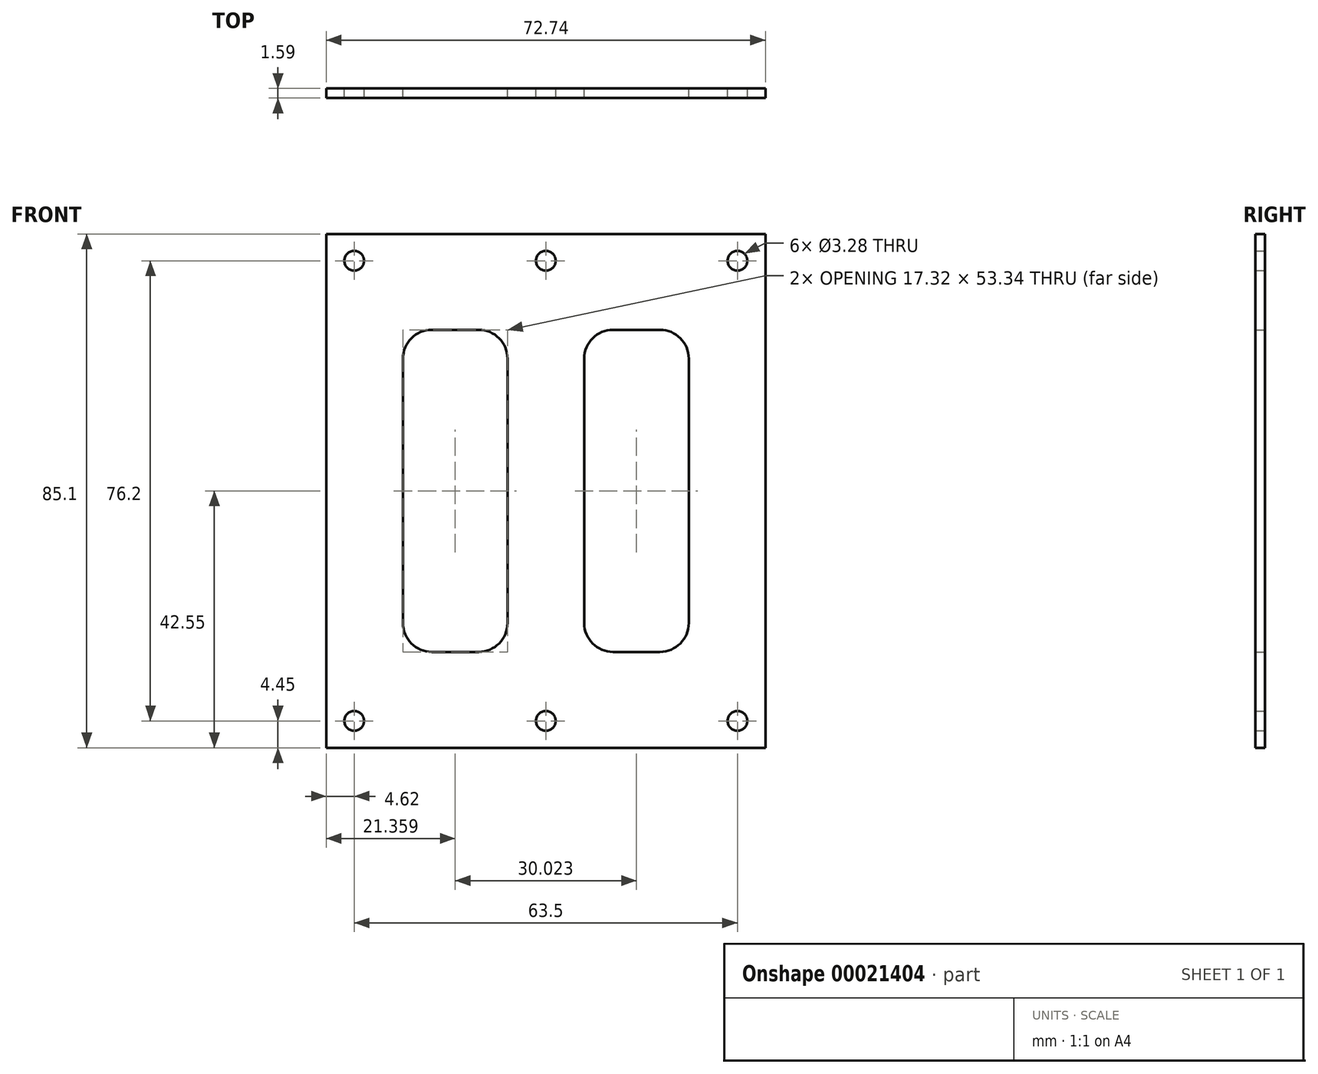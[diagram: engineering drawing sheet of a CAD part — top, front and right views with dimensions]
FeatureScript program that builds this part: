
annotation { "Feature Type Name" : "Feature", "Feature Type Description" : "" }
export const myFeature = defineFeature(function(context is Context, id is Id, definition is map)
    precondition{}
    {
        {
            var Q0;
            Q0=qCreatedBy(makeId("Front.planeOp"),FACE);
            var sketch = newSketch(context, id + "F0", { "sketchPlane" : qUnion([Q0])});
            skLineSegment(sketch, "E0.rect.bottom", {"start": v(36.37, 42.55) * mm, "end": v(-36.37, 42.55) * mm});
            skLineSegment(sketch, "E0.rect.top", {"start": v(36.37, -42.55) * mm, "end": v(-36.37, -42.55) * mm});
            skLineSegment(sketch, "E0.rect.left", {"start": v(36.37, 42.55) * mm, "end": v(36.37, -42.55) * mm});
            skLineSegment(sketch, "E0.rect.right", {"start": v(-36.37, 42.55) * mm, "end": v(-36.37, -42.55) * mm});
            skPoint(sketch, "E0.rect.middle", {"position": v(0, 0) * mm});
            skLineSegment(sketch, "E1.bottom", {"start": v(-23.67, 26.67) * mm, "end": v(-6.35, 26.67) * mm});
            skLineSegment(sketch, "E1.top", {"start": v(-23.67, -26.67) * mm, "end": v(-6.35, -26.67) * mm});
            skLineSegment(sketch, "E1.left", {"start": v(-23.67, 26.67) * mm, "end": v(-23.67, -26.67) * mm});
            skLineSegment(sketch, "E1.right", {"start": v(-6.35, 26.67) * mm, "end": v(-6.35, -26.67) * mm});
            skLineSegment(sketch, "E2.bottom", {"start": v(6.35, 26.67) * mm, "end": v(23.67, 26.67) * mm});
            skLineSegment(sketch, "E2.top", {"start": v(6.35, -26.67) * mm, "end": v(23.67, -26.67) * mm});
            skLineSegment(sketch, "E2.left", {"start": v(6.35, 26.67) * mm, "end": v(6.35, -26.67) * mm});
            skLineSegment(sketch, "E2.right", {"start": v(23.67, 26.67) * mm, "end": v(23.67, -26.67) * mm});
            skLineSegment(sketch, "E3", {"start": v(0, 0) * mm, "end": v(0, 48.78) * mm});
            skLineSegment(sketch, "E4", {"start": v(0, 0) * mm, "end": v(59.25, 0) * mm});
            skSolve(sketch);
        }
        {
            var Q0;
            {var subQ13=sQuery(id+"F0.wireOp",EDGE,"E0.rect.top");Q0=makeQuery(id+"F0.imprint","IMPRINT",FACE,{"disambiguationData":[TD([[makeQuery(id+"F0.imprint","IMPRINT",EDGE,{"derivedFrom":subQ13}),-1.0]])]});}
            var Q1;
            {var subQ7=sQuery(id+"F0.wireOp",EDGE,"E2.bottom");Q1=makeQuery(id+"F0.imprint","IMPRINT",FACE,{"disambiguationData":[TD([[makeQuery(id+"F0.imprint","IMPRINT",EDGE,{"derivedFrom":subQ7}),1.0]])]});}
            extrude(context, id + "F1", {"entities" : qUnion([Q0, Q1]), "depth" : 1.59 * mm});
        }
        {
            var Q0;
            Q0=makeQuery(id+"F1.opExtrude","SWEPT_EDGE",EDGE,{"disambiguationData":[OSD([sQuery(id+"F0.wireOp",EDGE,"E2.bottom"),sQuery(id+"F0.wireOp",EDGE,"E2.right")])]});
            var Q1;
            Q1=makeQuery(id+"F1.opExtrude","SWEPT_EDGE",EDGE,{"disambiguationData":[OSD([sQuery(id+"F0.wireOp",EDGE,"E2.top"),sQuery(id+"F0.wireOp",EDGE,"E2.right")])]});
            var Q2;
            Q2=makeQuery(id+"F1.opExtrude","SWEPT_EDGE",EDGE,{"disambiguationData":[OSD([sQuery(id+"F0.wireOp",EDGE,"E2.bottom"),sQuery(id+"F0.wireOp",EDGE,"E2.left")])]});
            var Q3;
            Q3=makeQuery(id+"F1.opExtrude","SWEPT_EDGE",EDGE,{"disambiguationData":[OSD([sQuery(id+"F0.wireOp",EDGE,"E2.top"),sQuery(id+"F0.wireOp",EDGE,"E2.left")])]});
            var Q4;
            Q4=makeQuery(id+"F1.opExtrude","SWEPT_EDGE",EDGE,{"disambiguationData":[OSD([sQuery(id+"F0.wireOp",EDGE,"E1.top"),sQuery(id+"F0.wireOp",EDGE,"E1.left")])]});
            var Q5;
            Q5=makeQuery(id+"F1.opExtrude","SWEPT_EDGE",EDGE,{"disambiguationData":[OSD([sQuery(id+"F0.wireOp",EDGE,"E1.bottom"),sQuery(id+"F0.wireOp",EDGE,"E1.left")])]});
            var Q6;
            Q6=makeQuery(id+"F1.opExtrude","SWEPT_EDGE",EDGE,{"disambiguationData":[OSD([sQuery(id+"F0.wireOp",EDGE,"E1.bottom"),sQuery(id+"F0.wireOp",EDGE,"E1.right")])]});
            var Q7;
            Q7=makeQuery(id+"F1.opExtrude","SWEPT_EDGE",EDGE,{"disambiguationData":[OSD([sQuery(id+"F0.wireOp",EDGE,"E1.top"),sQuery(id+"F0.wireOp",EDGE,"E1.right")])]});
            fillet(context, id + "F2", {"entities" : qUnion([Q0, Q1, Q2, Q3, Q4, Q5, Q6, Q7]), "radius" : 4.78 * mm, "tangentPropagation" : true, "allowEdgeOverflow" : false});
        }
        {
            var Q0;
            Q0=qCreatedBy(makeId("Front.planeOp"),FACE);
            var sketch = newSketch(context, id + "F3", { "sketchPlane" : qUnion([Q0])});
            skLineSegment(sketch, "E5.rect.bottom", {"start": v(-31.75, 38.1) * mm, "end": v(31.75, 38.1) * mm});
            skLineSegment(sketch, "E5.rect.top", {"start": v(-31.75, -38.1) * mm, "end": v(31.75, -38.1) * mm});
            skLineSegment(sketch, "E5.rect.left", {"start": v(-31.75, 38.1) * mm, "end": v(-31.75, -38.1) * mm});
            skLineSegment(sketch, "E5.rect.right", {"start": v(31.75, 38.1) * mm, "end": v(31.75, -38.1) * mm});
            skPoint(sketch, "E5.rect.middle", {"position": v(0, 0) * mm});
            skLineSegment(sketch, "E6", {"start": v(0, 38.1) * mm, "end": v(0, 0) * mm});
            skLineSegment(sketch, "E7", {"start": v(0, -38.1) * mm, "end": v(0, 0) * mm});
            skSolve(sketch);
        }
        {
            var Q0;
            Q0=sQuery(id+"F3.wireOp",VERTEX,"E5.rect.bottom.start");
            var Q1;
            Q1=sQuery(id+"F3.wireOp",VERTEX,"E6.start");
            var Q2;
            Q2=sQuery(id+"F3.wireOp",VERTEX,"E5.rect.right.start");
            var Q3;
            Q3=sQuery(id+"F3.wireOp",VERTEX,"E5.rect.left.end");
            var Q4;
            Q4=sQuery(id+"F3.wireOp",VERTEX,"E7.start");
            var Q5;
            Q5=sQuery(id+"F3.wireOp",VERTEX,"E5.rect.right.end");
            var Q6;
            Q6=makeQuery(id+"F1.opExtrude","SWEPT_BODY",BODY,{"disambiguationData":[OSD([sQuery(id+"F0.wireOp",EDGE,"E0.rect.bottom"),sQuery(id+"F0.wireOp",EDGE,"E0.rect.top"),sQuery(id+"F0.wireOp",EDGE,"E0.rect.left"),sQuery(id+"F0.wireOp",EDGE,"E0.rect.right"),sQuery(id+"F0.wireOp",EDGE,"E1.bottom"),sQuery(id+"F0.wireOp",EDGE,"E1.top"),sQuery(id+"F0.wireOp",EDGE,"E1.left"),sQuery(id+"F0.wireOp",EDGE,"E1.right"),sQuery(id+"F0.wireOp",EDGE,"E2.bottom"),sQuery(id+"F0.wireOp",EDGE,"E2.top"),sQuery(id+"F0.wireOp",EDGE,"E2.left"),sQuery(id+"F0.wireOp",EDGE,"E2.right")])]});
            hole(context, id + "F4", {"style" : HoleStyle.SIMPLE, "holeDiameter" : 3.28 * mm, "endStyle" : HoleEndStyle.THROUGH, "oppositeDirection" : true, "locations" : qUnion([Q0, Q1, Q2, Q3, Q4, Q5]), "scope" : qUnion([Q6])});
        }
    });
